# Revit family: 29e14ea1_9282_4abc_942a_cb5f4206041e
name_source: partatom
category: Generic Models
revit_build: Autodesk Revit Architecture 2015 (Build: 20140606_1530(x64)
units: mm (PartAtom-declared; Revit-internal decimal feet)

## types (1)
- Default
    BIMobject category = Armchairs
    BOSUseNativeGeometries = 1
    Date of publishing = 9/5/2016
    Design country = Sweden
    Edition number = 1
    IFC Classification = Furniture
    Manufacturer country = Sweden
    Manufacturer name = Bl?? Station
    Material main = Upholstery
    Material secondary = Steel
    NBS Reference Code = 31-12
    NBS Reference Description = Chairs, Seats And Bench Seating
    Nominal height = 720
    Nominal width = 830
    Product Guid = a129fec4-7912-4f89-9b89-417ac7df1ede
    Product SKU = B30
    Product data url = https://bimobject.com
    Product family = Easy Chairs
    Product group = ??hus
    Product name = ??hus B30
    QR code = http://bimobject.com
    Uniclass 1.4 Code = L8211
    Uniclass 1.4 Description = Furniture
    Weight Net (Kg) = 15.7

## geometry (parser evidence)
native form markers: Sweep x3
no freeform markers — native parametric forms only
